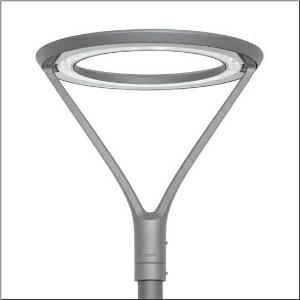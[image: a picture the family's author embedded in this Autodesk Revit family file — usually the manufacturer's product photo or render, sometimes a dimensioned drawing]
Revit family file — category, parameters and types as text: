
# Revit family: dl_r__20_led___pl1_2s_5xa51283ns008p_4f39
name_source: partatom
category: Lighting Fixtures
units: mm (PartAtom-declared; Revit-internal decimal feet)

## family parameters
Cut with Voids When Loaded = No
Host = Face
Light Source = No
Part Type = Normal
Room Calculation Point = No
Round Connector Dimension = Use Diameter
Shared = No

## types (1)
- --- (1 x LED 4000K / CRI = 80 (unbekannt), 5340 lm, 4000K)
    Apparent Load = 53 VA
    CIE Flux Codes = 34 78 98 100 100
    Color Rendering = 80
    Color Temperature = 4000K
    Default Elevation = 1800 mm
    Description = DL® 20 LED, mast luminaire, primary light control with reflector, highly specular, primary optical cover: cover, of toughened safety glass of clear glass with excellent transmission level, light distribution: PL1.2s, light emission: direct distribution, primary light characteristic: symmetric, installation type: post-top, LED High Power LED, rated luminous flux: 5.340 lm, light colour: 840, colour temperature: 4000K, control gear: ECG Plus, control: overheat protection, power reduction, digital communication interface, constant luminous flux control, time-dependent luminous flux control, flexible luminous flux parameterisation, electronic power reduction, mains connection: 220..240V, 50/60Hz, connection cable pre-assembled, cable length: 5 m, start of lifetime: 53 W, end of lifetime: 54 W, reduction: 24 W, luminaire housing, upper part, of cast aluminium, powder-coated, Siteco® metallic grey (DB 702S), diameter: 690 mm, height: 690mm, spigot size: 76mm (post-top), luminaire housing, of cast aluminium, powder-coated, Siteco® metallic grey (DB 702S), protection rating (complete): IP66, insulation class (complete): insulation class II (safety insulation), certification: CE, ENEC, VDE, impact resistance: IK08, permissible ambient temperature for indoor applications: -25..+30°C, standard-compliant lighting for roads and squares, packaging unit: 1 piece

Light Distribution: PL1.2s
    Height = 690 mm
    Lamp = 1 x LED 4000K / CRI >= 80 (unbekannt)
    Lamp Light Flux = 5340 lm
    Lamp count = 1
    Length = 690 mm
    Luminous efficacy = 101 lm/W
    Manufacturer = Siteco
    ModVariant = No
    Model = 5XA51283NS008P
    Number of Poles = 1
    OnlyDefault = Yes
    Power Factor = 1
    Product Name = DL® 20 LED | PL1.2s
    Product group = mast luminaire | pylon top
    ProductGroupID = 6100
    Protection Class = Protection class II
    Protection Degree = IP 66
    RLX_Detail_Level = 1
    RlxData = <blob elided: 203909 chars, md5=0a254393>
    Socket = socket
    Standby Power = 0 W
    System Light Flux = 5340 lm
    System Power = 53 W
    Type Comments = factory setting: luminous flux: 100 % | dim-lin: 254 | 683 mA
    Type Image = l_1006001.jpg
    URL = http://relux.com
    VarID = @adj_141527
    Voltage = 0 V
    Weight = 0.00 kg
    Width = 0 mm  [stored 0 ft]

note: [stored X ft] marks values corroborated as IEEE doubles in the binary element streams (Revit-internal decimal feet)

## geometry (parser evidence)
native form markers: Blend x4, Sweep x8
no freeform markers — native parametric forms only
